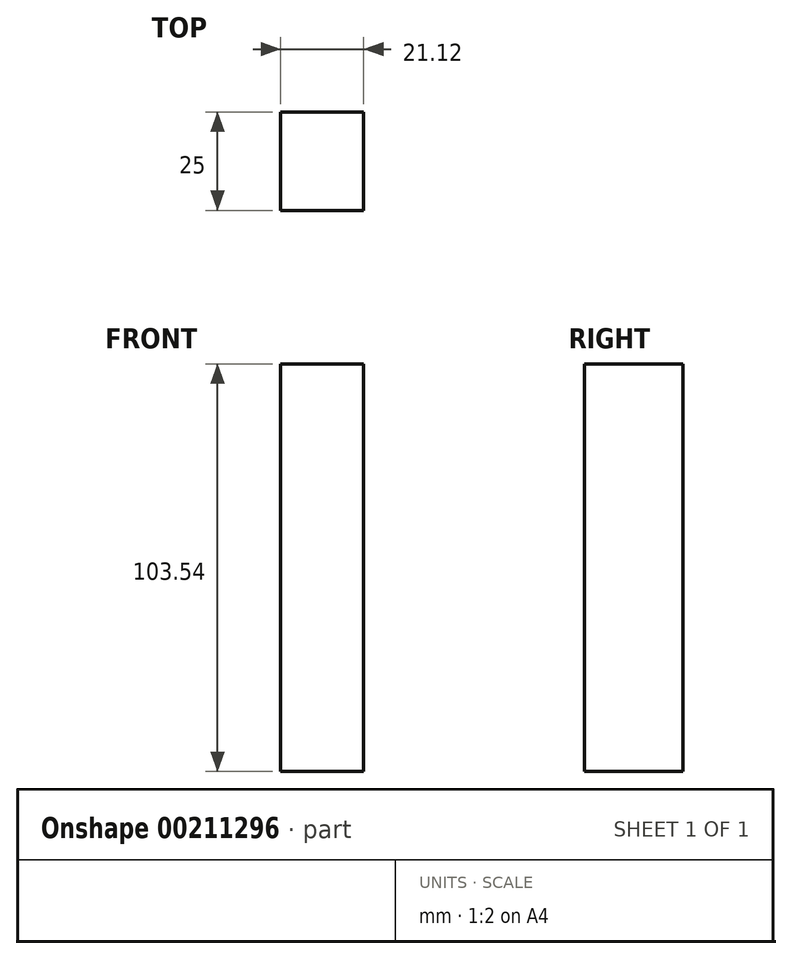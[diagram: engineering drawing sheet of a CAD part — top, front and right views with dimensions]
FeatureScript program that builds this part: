
annotation { "Feature Type Name" : "Feature", "Feature Type Description" : "" }
export const myFeature = defineFeature(function(context is Context, id is Id, definition is map)
    precondition{}
    {
        {
            var Q0;
            Q0=qCreatedBy(makeId("Front.planeOp"),FACE);
            var sketch = newSketch(context, id + "F0", { "sketchPlane" : qUnion([Q0])});
            skLineSegment(sketch, "E0.bottom", {"start": v(-10.56, 51.77) * mm, "end": v(10.56, 51.77) * mm});
            skLineSegment(sketch, "E0.top", {"start": v(-10.56, -51.77) * mm, "end": v(10.56, -51.77) * mm});
            skLineSegment(sketch, "E0.left", {"start": v(-10.56, 51.77) * mm, "end": v(-10.56, -51.77) * mm});
            skLineSegment(sketch, "E0.right", {"start": v(10.56, 51.77) * mm, "end": v(10.56, -51.77) * mm});
            skPoint(sketch, "E0.middle", {"position": v(0, 0) * mm});
            skSolve(sketch);
        }
        {
            var Q0;
            Q0=makeQuery(id+"F0.imprint","IMPRINT",FACE,{"disambiguationData":[TD([[makeQuery(id+"F0.imprint","IMPRINT",EDGE,{"derivedFrom":sQuery(id+"F0.wireOp",EDGE,"E0.bottom")}),-1.0]])]});
            extrude(context, id + "F1", {"entities" : qUnion([Q0]), "depth" : 25 * mm});
        }
    });
